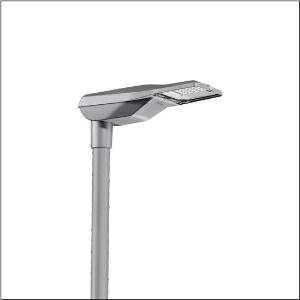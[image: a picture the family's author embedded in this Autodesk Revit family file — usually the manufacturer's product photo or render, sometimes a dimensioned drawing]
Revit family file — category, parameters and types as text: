
# Revit family: streetlight_sl_21_iq_micro___stw1_0a_5xe1e31g08db_041b
name_source: partatom
category: Lighting Fixtures
units: mm (PartAtom-declared; Revit-internal decimal feet)

## family parameters
Cut with Voids When Loaded = No
Host = Face
Light Source = No
Part Type = Normal
Room Calculation Point = No
Round Connector Dimension = Use Diameter
Shared = No

## types (1)
- --- (1 x LED, 4810 lm, 36.4 W, 3000K)
    Apparent Load = 36 VA
    CIE Flux Codes = 38 75 98 100 100
    Color Rendering = 70
    Color Temperature = 3000K
    Default Elevation = 1800 mm
    Description = Streetlight SL 21 iQ micro, mast luminaire, primary light control with lens, of PMMA, primary optical cover: cover, of toughened safety glass, transparent, light distribution: STW1.0a, light emission: direct distribution, primary light characteristic: asymmetric, installation type: post-top, side-entry, LED, High Power LED, rated luminous flux: 4.810lm, luminous efficacy: 132lm/W, light colour: 730, colour temperature: 3000K, control: Street-Remote, Auto-Match, Temp-Guard, Lumen-Switch, Night-Set, Smart-Wire, Light-Fading, Desk-Remote (wireless, voltage-free reading and setting of iQ features in the workshop via application-optimized NFC function/RFID function), optimised constant luminous flux control (CLO 2.0), presetting dimming linear, mains connection: 220..240V, AC, 50/60Hz, start of lifetime: 36W, end of service life: 38W, reduction: 16W, luminaire housing, of diecast aluminium, powder-coated, Siteco® metallic grey (DB 702S), corrosivity category C5 mid according to DIN EN ISO 12944, please order mast flange separately, inclination adjustable: 0°, 5°, 10°, 15°, sealing non-destructively replaceable, multi-level sealing system, length: 528mm, width: 235mm, height: 110mm, mast flange for spigot size: 42mm (side-entry): 5XC10008XM4, 60/48mm (side-entry/post-top): 5XC10108XM2, 76/60mm (side-entry/post-top): 5XC10108XM1, protection rating (complete): IP66, insulation class (complete): insulation class II (safety insulation), certification: CE, ENEC, ENEC+, VDE, impact resistance: IK09, permissible operating ambient temperature for outdoor applications: -40..+50°C, standard-compliant lighting for roads and squares, packaging unit: 1 piece

Light Distribution: STW1.0a
    Height = 110 mm
    Lamp = 1 x LED
    Lamp Light Flux = 4810 lm
    Lamp Power = 36.4 W
    Lamp count = 1
    Length = 528 mm
    Luminous efficacy = 132 lm/W
    Manufacturer = Siteco
    ModVariant = No
    Model = 5XE1E31G08DB
    Number of Poles = 1
    OnlyDefault = Yes
    Power Factor = 1
    Product Name = Streetlight SL 21 iQ micro | STW1.0a
    Product group = mast luminaire | pylon top
    ProductGroupID = 6100
    Protection Class = Protection class II
    Protection Degree = IP 66
    RLX_Detail_Level = 1
    RLX_Emergency_Light_Flux = 0 lm
    RLX_Emergency_Type = 0
    RLX_Emergency_Type_DB = No
    RlxData = <blob elided: 99025 chars, md5=3dec8f2c>
    Socket = socket
    Standby Power = 0 W
    System Light Flux = 4810 lm
    System Power = 36 W
    Type Comments = factory setting: luminous flux: 100 % | dim-lin: 254 | 715 mA
    Type Image = l_1006881.jpg
    URL = http://relux.com
    VarID = @adj_087765
    Voltage = 0 V
    Weight = 0.00 kg
    Width = 235 mm

## geometry (parser evidence)
native form markers: Blend x4, Sweep x9
no freeform markers — native parametric forms only
